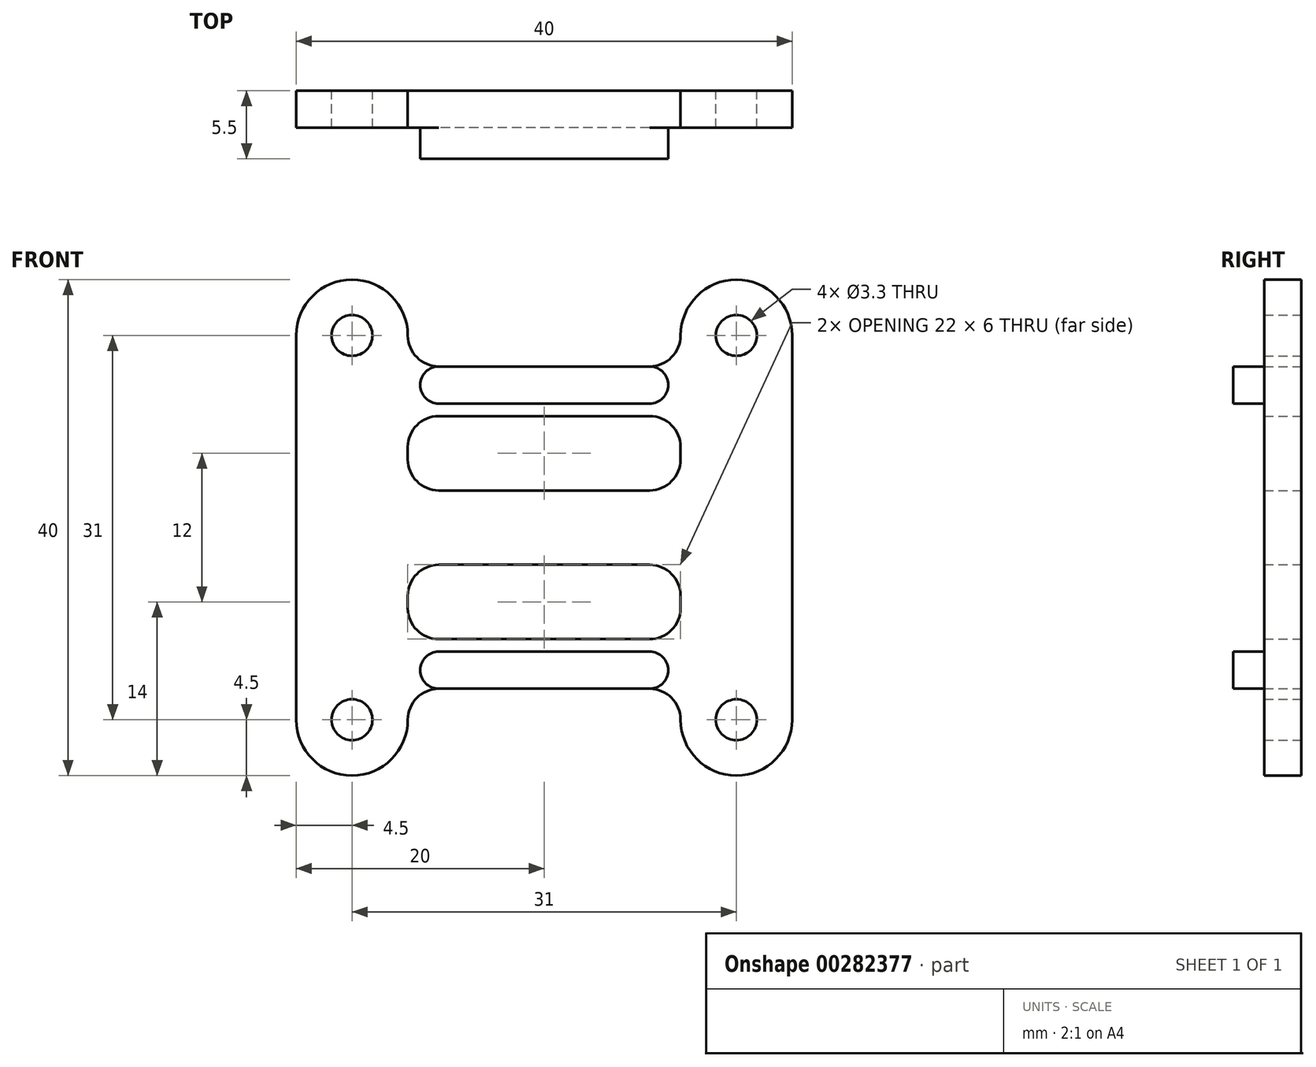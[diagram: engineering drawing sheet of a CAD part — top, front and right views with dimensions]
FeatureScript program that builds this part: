
annotation { "Feature Type Name" : "Feature", "Feature Type Description" : "" }
export const myFeature = defineFeature(function(context is Context, id is Id, definition is map)
    precondition{}
    {
        {
            var Q0;
            Q0=qCreatedBy(makeId("Front.planeOp"),FACE);
            var sketch = newSketch(context, id + "F0", { "sketchPlane" : qUnion([Q0])});
            skLineSegment(sketch, "E0.bottom", {"start": v(11, -15.5) * mm, "end": v(-11, -15.5) * mm, "construction": true});
            skLineSegment(sketch, "E0.top", {"start": v(11, 15.5) * mm, "end": v(-11, 15.5) * mm, "construction": true});
            skPoint(sketch, "E0.middle", {"position": v(0, 0) * mm});
            skCircle(sketch, "E1", {"center": v(-15.5, 15.5) * mm, "radius": 1.65 * mm});
            skArc(sketch, "E2", {"start": v(-11, 15.5) * mm, "mid": v(-15.5, 20) * mm, "end": v(-20, 15.5) * mm});
            skCircle(sketch, "E3", {"center": v(15.5, 15.5) * mm, "radius": 1.65 * mm});
            skArc(sketch, "E4", {"start": v(20, 15.5) * mm, "mid": v(15.5, 20) * mm, "end": v(11, 15.5) * mm});
            skArc(sketch, "E5", {"start": v(11, -15.5) * mm, "mid": v(15.5, -20) * mm, "end": v(20, -15.5) * mm});
            skCircle(sketch, "E6", {"center": v(15.5, -15.5) * mm, "radius": 1.65 * mm});
            skCircle(sketch, "E7", {"center": v(-15.5, -15.5) * mm, "radius": 1.65 * mm});
            skArc(sketch, "E8", {"start": v(-20, -15.5) * mm, "mid": v(-15.5, -20) * mm, "end": v(-11, -15.5) * mm});
            skLineSegment(sketch, "E9", {"start": v(8.5, -3) * mm, "end": v(-8.5, -3) * mm});
            skLineSegment(sketch, "E10", {"start": v(-11, -5.5) * mm, "end": v(-11, -6.5) * mm});
            skLineSegment(sketch, "E11", {"start": v(-8.5, -9) * mm, "end": v(8.5, -9) * mm});
            skLineSegment(sketch, "E12", {"start": v(11, -6.5) * mm, "end": v(11, -5.5) * mm});
            skPoint(sketch, "E13.visualSharp", {"position": v(-11, -3) * mm});
            skArc(sketch, "E13.filletArc", {"start": v(-8.5, -3) * mm, "mid": v(-10.27, -3.73) * mm, "end": v(-11, -5.5) * mm});
            skPoint(sketch, "E14.visualSharp", {"position": v(11, -3) * mm});
            skArc(sketch, "E14.filletArc", {"start": v(11, -5.5) * mm, "mid": v(10.27, -3.73) * mm, "end": v(8.5, -3) * mm});
            skPoint(sketch, "E15.visualSharp", {"position": v(11, -9) * mm});
            skArc(sketch, "E15.filletArc", {"start": v(8.5, -9) * mm, "mid": v(10.27, -8.27) * mm, "end": v(11, -6.5) * mm});
            skPoint(sketch, "E16.visualSharp", {"position": v(-11, -9) * mm});
            skArc(sketch, "E16.filletArc", {"start": v(-11, -6.5) * mm, "mid": v(-10.27, -8.27) * mm, "end": v(-8.5, -9) * mm});
            skLineSegment(sketch, "E17", {"start": v(15.5, 15.5) * mm, "end": v(20, 15.5) * mm, "construction": true});
            skLineSegment(sketch, "E18", {"start": v(20, 15.5) * mm, "end": v(20, -15.5) * mm});
            skLineSegment(sketch, "E19", {"start": v(-11, 15.5) * mm, "end": v(-11, 15.5) * mm});
            skLineSegment(sketch, "E20", {"start": v(-8.5, 13) * mm, "end": v(8.5, 13) * mm});
            skLineSegment(sketch, "E21", {"start": v(11, 15.5) * mm, "end": v(11, 15.5) * mm});
            skLineSegment(sketch, "E22", {"start": v(-11, -15.5) * mm, "end": v(-11, -15.5) * mm});
            skLineSegment(sketch, "E23", {"start": v(-8.5, -13) * mm, "end": v(8.5, -13) * mm});
            skLineSegment(sketch, "E24", {"start": v(11, -15.5) * mm, "end": v(11, -15.5) * mm});
            skPoint(sketch, "E25.visualSharp", {"position": v(-11, 13) * mm});
            skArc(sketch, "E25.filletArc", {"start": v(-11, 15.5) * mm, "mid": v(-10.27, 13.73) * mm, "end": v(-8.5, 13) * mm});
            skPoint(sketch, "E26.visualSharp", {"position": v(11, 13) * mm});
            skArc(sketch, "E26.filletArc", {"start": v(8.5, 13) * mm, "mid": v(10.27, 13.73) * mm, "end": v(11, 15.5) * mm});
            skPoint(sketch, "E27.visualSharp", {"position": v(-11, -13) * mm});
            skArc(sketch, "E27.filletArc", {"start": v(-8.5, -13) * mm, "mid": v(-10.27, -13.73) * mm, "end": v(-11, -15.5) * mm});
            skPoint(sketch, "E28.visualSharp", {"position": v(11, -13) * mm});
            skArc(sketch, "E28.filletArc", {"start": v(11, -15.5) * mm, "mid": v(10.27, -13.73) * mm, "end": v(8.5, -13) * mm});
            skLineSegment(sketch, "E29", {"start": v(-20, 15.5) * mm, "end": v(-20, -15.5) * mm});
            skLineSegment(sketch, "E30", {"start": v(-20, 0) * mm, "end": v(20, 0) * mm, "construction": true});
            skLineSegment(sketch, "E31", {"start": v(0, 0) * mm, "end": v(0, 13) * mm, "construction": true});
            skLineSegment(sketch, "E32", {"start": v(-8.5, 13) * mm, "end": v(-8.5, -13) * mm, "construction": true});
            skLineSegment(sketch, "E33", {"start": v(8.5, 13) * mm, "end": v(8.5, -13) * mm, "construction": true});
            skLineSegment(sketch, "E34.MirrorCS", {"start": v(8.5, 3) * mm, "end": v(-8.5, 3) * mm});
            skArc(sketch, "E35.MirrorCS", {"start": v(-8.5, 3) * mm, "mid": v(-10.27, 3.73) * mm, "end": v(-11, 5.5) * mm});
            skArc(sketch, "E36.MirrorCS", {"start": v(-11, 6.5) * mm, "mid": v(-10.27, 8.27) * mm, "end": v(-8.5, 9) * mm});
            skLineSegment(sketch, "E37.MirrorCS", {"start": v(-8.5, 9) * mm, "end": v(8.5, 9) * mm});
            skArc(sketch, "E38.MirrorCS", {"start": v(8.5, 9) * mm, "mid": v(10.27, 8.27) * mm, "end": v(11, 6.5) * mm});
            skArc(sketch, "E39.MirrorCS", {"start": v(11, 5.5) * mm, "mid": v(10.27, 3.73) * mm, "end": v(8.5, 3) * mm});
            skLineSegment(sketch, "E40.MirrorCS", {"start": v(11, 6.5) * mm, "end": v(11, 5.5) * mm});
            skLineSegment(sketch, "E41.MirrorCS", {"start": v(-11, 5.5) * mm, "end": v(-11, 6.5) * mm});
            skSolve(sketch);
        }
        {
            var Q0;
            Q0=qSketchRegion(id+"F0",true);
            extrude(context, id + "F1", {"entities" : qUnion([Q0]), "depth" : 3 * mm});
        }
        {
            var Q0;
            Q0=makeQuery(id+"F1.opExtrude","CAP_FACE",FACE,{"disambiguationData":[OSD([sQuery(id+"F0.wireOp",EDGE,"E0.right"),sQuery(id+"F0.wireOp",EDGE,"E1"),sQuery(id+"F0.wireOp",EDGE,"E2"),sQuery(id+"F0.wireOp",EDGE,"E3"),sQuery(id+"F0.wireOp",EDGE,"E4"),sQuery(id+"F0.wireOp",EDGE,"E5"),sQuery(id+"F0.wireOp",EDGE,"E6"),sQuery(id+"F0.wireOp",EDGE,"E7"),sQuery(id+"F0.wireOp",EDGE,"E8"),sQuery(id+"F0.wireOp",EDGE,"E9"),sQuery(id+"F0.wireOp",EDGE,"LVAo8Dzw-5Eew-AT70-Mw4X-mh2Fi7ab2uKk"),sQuery(id+"F0.wireOp",EDGE,"aae7adb9-b974-49f8-9ad6-26da6c713436.trimOffspring"),sQuery(id+"F0.wireOp",EDGE,"E10"),sQuery(id+"F0.wireOp",EDGE,"E11"),sQuery(id+"F0.wireOp",EDGE,"E12"),sQuery(id+"F0.wireOp",EDGE,"kV28CBRp-7BnM-A0mL-C1UT-glgtCk8OC8Bi"),sQuery(id+"F0.wireOp",EDGE,"ojZpAfz2-tPix-sQu2-gTRE-k6PYrLLaIgYI"),sQuery(id+"F0.wireOp",EDGE,"9BFbzIwF-mcko-boCK-71P3-hxh1gQcxN1p4"),sQuery(id+"F0.wireOp",EDGE,"0f3de939-d2dd-43fc-98b0-805f918ee65d.trimOffspring"),sQuery(id+"F0.wireOp",EDGE,"E13.filletArc"),sQuery(id+"F0.wireOp",EDGE,"E14.filletArc"),sQuery(id+"F0.wireOp",EDGE,"E15.filletArc"),sQuery(id+"F0.wireOp",EDGE,"E16.filletArc"),sQuery(id+"F0.wireOp",EDGE,"a4b2192d-02a0-4486-9522-b54895257421.filletArc"),sQuery(id+"F0.wireOp",EDGE,"65a6dfc5-2a0d-4b36-98e8-d6037f465be3.filletArc"),sQuery(id+"F0.wireOp",EDGE,"932fd38c-c3a0-4d4f-a037-8091e868a1ac.filletArc"),sQuery(id+"F0.wireOp",EDGE,"3b14f0d2-c8a5-4b0f-89c2-3dd0a946f87a.filletArc"),sQuery(id+"F0.wireOp",EDGE,"E18"),sQuery(id+"F0.wireOp",EDGE,"x4UfDSdM-hSlM-MX5K-l1IV-Jibow3xHNd0Y"),sQuery(id+"F0.wireOp",EDGE,"8zIixXxZ-WWGH-xri6-fnmr-eko2Lxea7znz"),sQuery(id+"F0.wireOp",EDGE,"E20"),sQuery(id+"F0.wireOp",EDGE,"E23"),sQuery(id+"F0.wireOp",EDGE,"E25.filletArc"),sQuery(id+"F0.wireOp",EDGE,"E26.filletArc"),sQuery(id+"F0.wireOp",EDGE,"E27.filletArc"),sQuery(id+"F0.wireOp",EDGE,"E28.filletArc"),sQuery(id+"F0.wireOp",EDGE,"jbr3fW3x-2yhg-9aY5-g6jk-Y18SqahvBJEi"),sQuery(id+"F0.wireOp",EDGE,"sUcubdSR-DOk7-hDrT-qJ0N-BrkZJNtFdqSF")])],"isStart":false});
            var sketch = newSketch(context, id + "F2", { "sketchPlane" : qUnion([Q0])});
            skCircle(sketch, "E42", {"center": v(-15.5, 15.5) * mm, "radius": 4.5 * mm, "construction": true});
            skCircle(sketch, "E43", {"center": v(15.5, 15.5) * mm, "radius": 4.5 * mm, "construction": true});
            skCircle(sketch, "E44", {"center": v(15.5, -15.5) * mm, "radius": 4.5 * mm, "construction": true});
            skCircle(sketch, "E45", {"center": v(-15.5, -15.5) * mm, "radius": 4.5 * mm, "construction": true});
            skLineSegment(sketch, "E46", {"start": v(-8.5, -10) * mm, "end": v(8.5, -10) * mm});
            skLineSegment(sketch, "E47", {"start": v(15.5, 15.5) * mm, "end": v(15.5, -15.5) * mm, "construction": true});
            skLineSegment(sketch, "E48", {"start": v(-8.5, -13) * mm, "end": v(8.5, -13) * mm});
            skLineSegment(sketch, "E49", {"start": v(-8.5, -13) * mm, "end": v(-8.5, -10) * mm, "construction": true});
            skLineSegment(sketch, "E50", {"start": v(8.5, -13) * mm, "end": v(8.5, -10) * mm, "construction": true});
            skArc(sketch, "E51", {"start": v(-8.5, -10) * mm, "mid": v(-10, -11.5) * mm, "end": v(-8.5, -13) * mm});
            skArc(sketch, "E52", {"start": v(8.5, -13) * mm, "mid": v(10, -11.5) * mm, "end": v(8.5, -10) * mm});
            skLineSegment(sketch, "E53", {"start": v(0, 0) * mm, "end": v(15.5, 0) * mm, "construction": true});
            skLineSegment(sketch, "E54.MirrorCS", {"start": v(-8.5, 10) * mm, "end": v(8.5, 10) * mm});
            skArc(sketch, "E55.MirrorCS", {"start": v(-8.5, 10) * mm, "mid": v(-10, 11.5) * mm, "end": v(-8.5, 13) * mm});
            skLineSegment(sketch, "E56.MirrorCS", {"start": v(-8.5, 13) * mm, "end": v(8.5, 13) * mm});
            skArc(sketch, "E57.MirrorCS", {"start": v(8.5, 13) * mm, "mid": v(10, 11.5) * mm, "end": v(8.5, 10) * mm});
            skSolve(sketch);
        }
        {
            var Q0;
            Q0=qSketchRegion(id+"F2",true);
            extrude(context, id + "F3", {"entities" : qUnion([Q0]), "operationType" : NewBodyOperationType.ADD, "depth" : 2.5 * mm});
        }
    });
